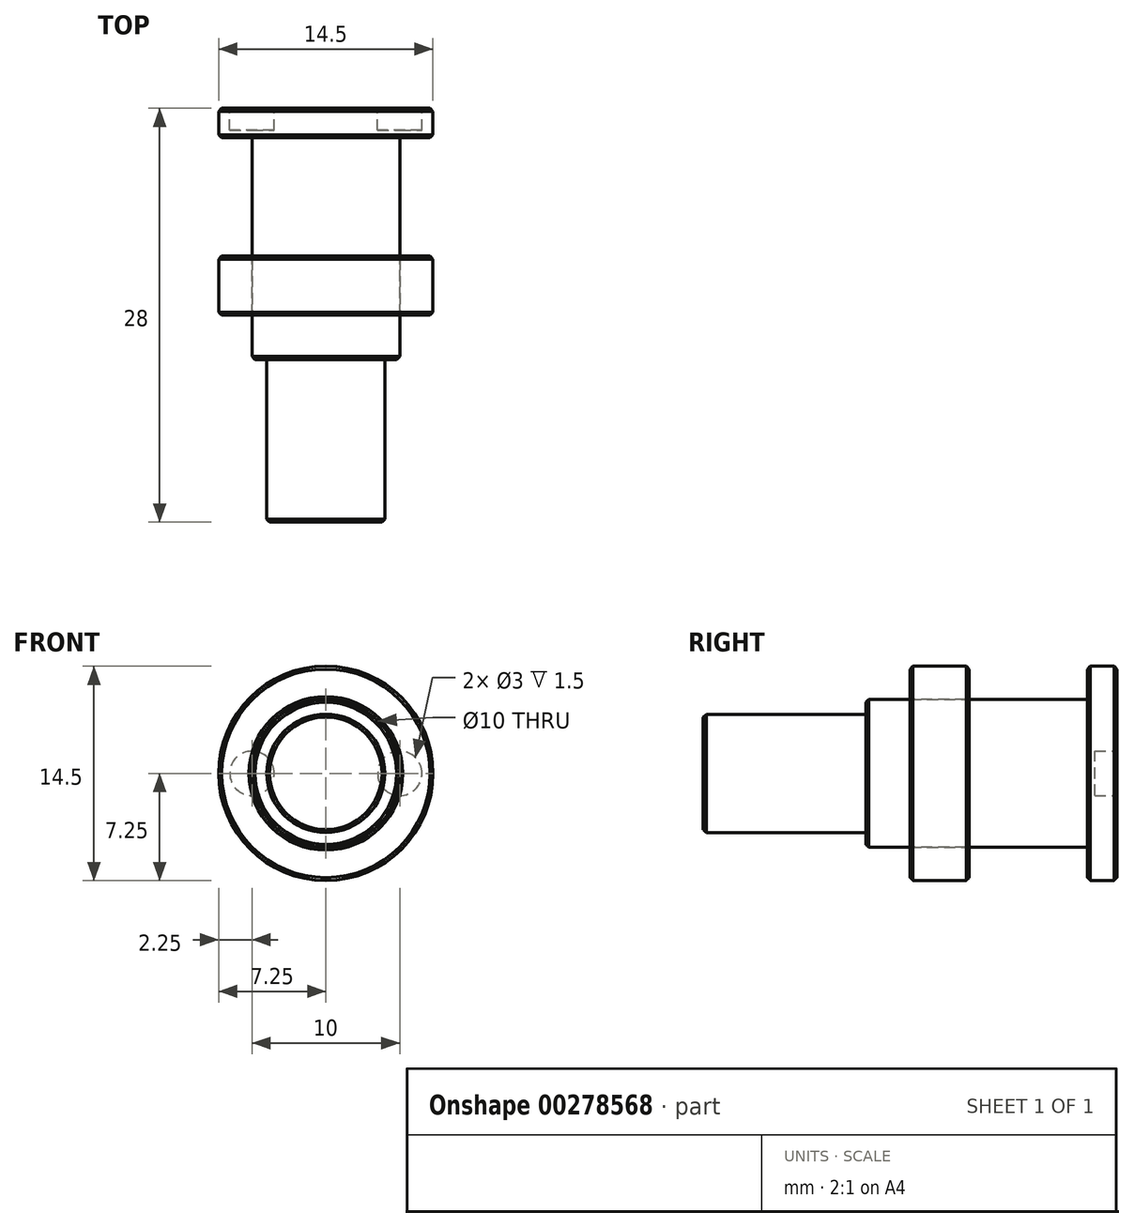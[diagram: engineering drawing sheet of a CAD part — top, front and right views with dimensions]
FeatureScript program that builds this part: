
annotation { "Feature Type Name" : "Feature", "Feature Type Description" : "" }
export const myFeature = defineFeature(function(context is Context, id is Id, definition is map)
    precondition{}
    {
        {
            var Q0;
            Q0=qCreatedBy(makeId("Front.planeOp"),FACE);
            var sketch = newSketch(context, id + "F0", { "sketchPlane" : qUnion([Q0])});
            skCircle(sketch, "E0", {"center": v(0, 0) * mm, "radius": 7.25 * mm});
            skCircle(sketch, "E1", {"center": v(0, 0) * mm, "radius": 5 * mm});
            skCircle(sketch, "E2", {"center": v(0, 0) * mm, "radius": 4 * mm});
            skCircle(sketch, "E3", {"center": v(5, 0) * mm, "radius": 1.5 * mm});
            skCircle(sketch, "E4.1.1", {"center": v(-5, 0) * mm, "radius": 1.5 * mm});
            skSolve(sketch);
        }
        {
            var Q0;
            Q0=makeQuery(id+"F0.imprint","IMPRINT",FACE,{"disambiguationData":[TD([[makeQuery(id+"F0.imprint","IMPRINT",EDGE,{"derivedFrom":sQuery(id+"F0.wireOp",EDGE,"E0")}),1.0]])]});
            var Q1;
            Q1=makeQuery(id+"F0.imprint","IMPRINT",FACE,{"disambiguationData":[TD([[makeQuery(id+"F0.imprint","IMPRINT",EDGE,{"derivedFrom":sQuery(id+"F0.wireOp",EDGE,"E1")}),1.0]])]});
            var Q2;
            Q2=makeQuery(id+"F0.imprint","IMPRINT",FACE,{"disambiguationData":[TD([[makeQuery(id+"F0.imprint","IMPRINT",EDGE,{"derivedFrom":sQuery(id+"F0.wireOp",EDGE,"E0")}),1.0]])]});
            var Q3;
            {var subQ0=sQuery(id+"F0.wireOp",EDGE,"E4.1.1");var subQ1=sQuery(id+"F0.wireOp",EDGE,"E1");var subQ2=makeQuery(id+"F0.imprint","INTERSECT",VERTEX,{"disambiguationData":[OD(0.0)],"derivedFrom":[subQ1,subQ0]});Q3=makeQuery(id+"F0.imprint","IMPRINT",FACE,{"disambiguationData":[TD([[makeQuery(id+"F0.imprint","IMPRINT",EDGE,{"disambiguationData":[TD([[subQ2,-1.0]])],"derivedFrom":subQ1}),-1.0]])]});}
            var Q4;
            {var subQ0=sQuery(id+"F0.wireOp",EDGE,"E3");var subQ1=sQuery(id+"F0.wireOp",EDGE,"E1");var subQ2=makeQuery(id+"F0.imprint","INTERSECT",VERTEX,{"disambiguationData":[OD(0.0)],"derivedFrom":[subQ1,subQ0]});Q4=makeQuery(id+"F0.imprint","IMPRINT",FACE,{"disambiguationData":[TD([[makeQuery(id+"F0.imprint","IMPRINT",EDGE,{"disambiguationData":[TD([[subQ2,1.0]])],"derivedFrom":subQ1}),1.0]])]});}
            var Q5;
            {var subQ0=sQuery(id+"F0.wireOp",EDGE,"E3");var subQ1=sQuery(id+"F0.wireOp",EDGE,"E1");var subQ2=makeQuery(id+"F0.imprint","INTERSECT",VERTEX,{"disambiguationData":[OD(0.0)],"derivedFrom":[subQ1,subQ0]});Q5=makeQuery(id+"F0.imprint","IMPRINT",FACE,{"disambiguationData":[TD([[makeQuery(id+"F0.imprint","IMPRINT",EDGE,{"disambiguationData":[TD([[subQ2,1.0]])],"derivedFrom":subQ1}),-1.0]])]});}
            var Q6;
            {var subQ0=sQuery(id+"F0.wireOp",EDGE,"E4.1.1");var subQ1=sQuery(id+"F0.wireOp",EDGE,"E1");var subQ2=makeQuery(id+"F0.imprint","INTERSECT",VERTEX,{"disambiguationData":[OD(0.0)],"derivedFrom":[subQ1,subQ0]});Q6=makeQuery(id+"F0.imprint","IMPRINT",FACE,{"disambiguationData":[TD([[makeQuery(id+"F0.imprint","IMPRINT",EDGE,{"disambiguationData":[TD([[subQ2,-1.0]])],"derivedFrom":subQ1}),1.0]])]});}
            var Q7;
            {var subQ0=sQuery(id+"F0.wireOp",EDGE,"E3");var subQ1=sQuery(id+"F0.wireOp",EDGE,"E2");var subQ2=makeQuery(id+"F0.imprint","INTERSECT",VERTEX,{"disambiguationData":[OD(0.0)],"derivedFrom":[subQ1,subQ0]});Q7=makeQuery(id+"F0.imprint","IMPRINT",FACE,{"disambiguationData":[TD([[makeQuery(id+"F0.imprint","IMPRINT",EDGE,{"disambiguationData":[TD([[subQ2,1.0]])],"derivedFrom":subQ1}),1.0]])]});}
            var Q8;
            {var subQ0=sQuery(id+"F0.wireOp",EDGE,"E4.1.1");var subQ1=sQuery(id+"F0.wireOp",EDGE,"E2");var subQ2=makeQuery(id+"F0.imprint","INTERSECT",VERTEX,{"disambiguationData":[OD(0.0)],"derivedFrom":[subQ1,subQ0]});Q8=makeQuery(id+"F0.imprint","IMPRINT",FACE,{"disambiguationData":[TD([[makeQuery(id+"F0.imprint","IMPRINT",EDGE,{"disambiguationData":[TD([[subQ2,-1.0]])],"derivedFrom":subQ1}),1.0]])]});}
            var Q9;
            {var subQ0=sQuery(id+"F0.wireOp",EDGE,"E4.1.1");var subQ1=sQuery(id+"F0.wireOp",EDGE,"E2");var subQ2=makeQuery(id+"F0.imprint","INTERSECT",VERTEX,{"disambiguationData":[OD(0.0)],"derivedFrom":[subQ1,subQ0]});Q9=makeQuery(id+"F0.imprint","IMPRINT",FACE,{"disambiguationData":[TD([[makeQuery(id+"F0.imprint","IMPRINT",EDGE,{"disambiguationData":[TD([[subQ2,1.0]])],"derivedFrom":subQ1}),1.0]])]});}
            extrude(context, id + "F1", {"entities" : qUnion([Q0, Q1, Q2, Q3, Q4, Q5, Q6, Q7, Q8, Q9]), "depth" : 2 * mm});
        }
        {
            var Q0;
            {var subQ0=sQuery(id+"F0.wireOp",EDGE,"E4.1.1");var subQ1=sQuery(id+"F0.wireOp",EDGE,"E2");var subQ2=makeQuery(id+"F0.imprint","INTERSECT",VERTEX,{"disambiguationData":[OD(0.0)],"derivedFrom":[subQ1,subQ0]});Q0=makeQuery(id+"F0.imprint","IMPRINT",FACE,{"disambiguationData":[TD([[makeQuery(id+"F0.imprint","IMPRINT",EDGE,{"disambiguationData":[TD([[subQ2,1.0]])],"derivedFrom":subQ1}),1.0]])]});}
            var Q1;
            {var subQ0=sQuery(id+"F0.wireOp",EDGE,"E3");var subQ1=sQuery(id+"F0.wireOp",EDGE,"E2");var subQ2=makeQuery(id+"F0.imprint","INTERSECT",VERTEX,{"disambiguationData":[OD(0.0)],"derivedFrom":[subQ1,subQ0]});Q1=makeQuery(id+"F0.imprint","IMPRINT",FACE,{"disambiguationData":[TD([[makeQuery(id+"F0.imprint","IMPRINT",EDGE,{"disambiguationData":[TD([[subQ2,1.0]])],"derivedFrom":subQ1}),1.0]])]});}
            var Q2;
            {var subQ0=sQuery(id+"F0.wireOp",EDGE,"E4.1.1");var subQ1=sQuery(id+"F0.wireOp",EDGE,"E1");var subQ2=makeQuery(id+"F0.imprint","INTERSECT",VERTEX,{"disambiguationData":[OD(1.0)],"derivedFrom":[subQ1,subQ0]});Q2=makeQuery(id+"F0.imprint","IMPRINT",FACE,{"disambiguationData":[TD([[makeQuery(id+"F0.imprint","IMPRINT",EDGE,{"disambiguationData":[TD([[subQ2,-1.0]])],"derivedFrom":subQ1}),1.0]])]});}
            var Q3;
            {var subQ0=sQuery(id+"F0.wireOp",EDGE,"E4.1.1");var subQ1=sQuery(id+"F0.wireOp",EDGE,"E1");var subQ2=makeQuery(id+"F0.imprint","INTERSECT",VERTEX,{"disambiguationData":[OD(0.0)],"derivedFrom":[subQ1,subQ0]});Q3=makeQuery(id+"F0.imprint","IMPRINT",FACE,{"disambiguationData":[TD([[makeQuery(id+"F0.imprint","IMPRINT",EDGE,{"disambiguationData":[TD([[subQ2,1.0]])],"derivedFrom":subQ1}),1.0]])]});}
            var Q4;
            {var subQ0=sQuery(id+"F0.wireOp",EDGE,"E4.1.1");var subQ1=sQuery(id+"F0.wireOp",EDGE,"E2");var subQ2=makeQuery(id+"F0.imprint","INTERSECT",VERTEX,{"disambiguationData":[OD(0.0)],"derivedFrom":[subQ1,subQ0]});Q4=makeQuery(id+"F0.imprint","IMPRINT",FACE,{"disambiguationData":[TD([[makeQuery(id+"F0.imprint","IMPRINT",EDGE,{"disambiguationData":[TD([[subQ2,-1.0]])],"derivedFrom":subQ1}),1.0]])]});}
            var Q5;
            {var subQ0=sQuery(id+"F0.wireOp",EDGE,"E4.1.1");var subQ1=sQuery(id+"F0.wireOp",EDGE,"E1");var subQ2=makeQuery(id+"F0.imprint","INTERSECT",VERTEX,{"disambiguationData":[OD(0.0)],"derivedFrom":[subQ1,subQ0]});Q5=makeQuery(id+"F0.imprint","IMPRINT",FACE,{"disambiguationData":[TD([[makeQuery(id+"F0.imprint","IMPRINT",EDGE,{"disambiguationData":[TD([[subQ2,-1.0]])],"derivedFrom":subQ1}),1.0]])]});}
            var Q6;
            {var subQ0=sQuery(id+"F0.wireOp",EDGE,"E3");var subQ1=sQuery(id+"F0.wireOp",EDGE,"E1");var subQ2=makeQuery(id+"F0.imprint","INTERSECT",VERTEX,{"disambiguationData":[OD(0.0)],"derivedFrom":[subQ1,subQ0]});Q6=makeQuery(id+"F0.imprint","IMPRINT",FACE,{"disambiguationData":[TD([[makeQuery(id+"F0.imprint","IMPRINT",EDGE,{"disambiguationData":[TD([[subQ2,1.0]])],"derivedFrom":subQ1}),1.0]])]});}
            extrude(context, id + "F2", {"entities" : qUnion([Q0, Q1, Q2, Q3, Q4, Q5, Q6]), "operationType" : NewBodyOperationType.ADD, "depth" : 17 * mm});
        }
        {
            var Q0;
            {var subQ0=sQuery(id+"F0.wireOp",EDGE,"E3");var subQ1=sQuery(id+"F0.wireOp",EDGE,"E2");var subQ2=makeQuery(id+"F0.imprint","INTERSECT",VERTEX,{"disambiguationData":[OD(0.0)],"derivedFrom":[subQ1,subQ0]});Q0=makeQuery(id+"F0.imprint","IMPRINT",FACE,{"disambiguationData":[TD([[makeQuery(id+"F0.imprint","IMPRINT",EDGE,{"disambiguationData":[TD([[subQ2,1.0]])],"derivedFrom":subQ1}),1.0]])]});}
            var Q1;
            {var subQ0=sQuery(id+"F0.wireOp",EDGE,"E4.1.1");var subQ1=sQuery(id+"F0.wireOp",EDGE,"E2");var subQ2=makeQuery(id+"F0.imprint","INTERSECT",VERTEX,{"disambiguationData":[OD(0.0)],"derivedFrom":[subQ1,subQ0]});Q1=makeQuery(id+"F0.imprint","IMPRINT",FACE,{"disambiguationData":[TD([[makeQuery(id+"F0.imprint","IMPRINT",EDGE,{"disambiguationData":[TD([[subQ2,1.0]])],"derivedFrom":subQ1}),1.0]])]});}
            var Q2;
            {var subQ0=sQuery(id+"F0.wireOp",EDGE,"E4.1.1");var subQ1=sQuery(id+"F0.wireOp",EDGE,"E2");var subQ2=makeQuery(id+"F0.imprint","INTERSECT",VERTEX,{"disambiguationData":[OD(0.0)],"derivedFrom":[subQ1,subQ0]});Q2=makeQuery(id+"F0.imprint","IMPRINT",FACE,{"disambiguationData":[TD([[makeQuery(id+"F0.imprint","IMPRINT",EDGE,{"disambiguationData":[TD([[subQ2,-1.0]])],"derivedFrom":subQ1}),1.0]])]});}
            extrude(context, id + "F3", {"entities" : qUnion([Q0, Q1, Q2]), "operationType" : NewBodyOperationType.ADD, "depth" : 28 * mm});
        }
        {
            var Q0;
            {var subQ0=sQuery(id+"F0.wireOp",EDGE,"E4.1.1");var subQ1=sQuery(id+"F0.wireOp",EDGE,"E2");var subQ2=makeQuery(id+"F0.imprint","INTERSECT",VERTEX,{"disambiguationData":[OD(0.0)],"derivedFrom":[subQ1,subQ0]});Q0=makeQuery(id+"F0.imprint","IMPRINT",FACE,{"disambiguationData":[TD([[makeQuery(id+"F0.imprint","IMPRINT",EDGE,{"disambiguationData":[TD([[subQ2,-1.0]])],"derivedFrom":subQ1}),1.0]])]});}
            var Q1;
            {var subQ0=sQuery(id+"F0.wireOp",EDGE,"E4.1.1");var subQ1=sQuery(id+"F0.wireOp",EDGE,"E1");var subQ2=makeQuery(id+"F0.imprint","INTERSECT",VERTEX,{"disambiguationData":[OD(0.0)],"derivedFrom":[subQ1,subQ0]});Q1=makeQuery(id+"F0.imprint","IMPRINT",FACE,{"disambiguationData":[TD([[makeQuery(id+"F0.imprint","IMPRINT",EDGE,{"disambiguationData":[TD([[subQ2,-1.0]])],"derivedFrom":subQ1}),1.0]])]});}
            var Q2;
            {var subQ0=sQuery(id+"F0.wireOp",EDGE,"E3");var subQ1=sQuery(id+"F0.wireOp",EDGE,"E1");var subQ2=makeQuery(id+"F0.imprint","INTERSECT",VERTEX,{"disambiguationData":[OD(0.0)],"derivedFrom":[subQ1,subQ0]});Q2=makeQuery(id+"F0.imprint","IMPRINT",FACE,{"disambiguationData":[TD([[makeQuery(id+"F0.imprint","IMPRINT",EDGE,{"disambiguationData":[TD([[subQ2,1.0]])],"derivedFrom":subQ1}),-1.0]])]});}
            var Q3;
            {var subQ0=sQuery(id+"F0.wireOp",EDGE,"E3");var subQ1=sQuery(id+"F0.wireOp",EDGE,"E1");var subQ2=makeQuery(id+"F0.imprint","INTERSECT",VERTEX,{"disambiguationData":[OD(0.0)],"derivedFrom":[subQ1,subQ0]});Q3=makeQuery(id+"F0.imprint","IMPRINT",FACE,{"disambiguationData":[TD([[makeQuery(id+"F0.imprint","IMPRINT",EDGE,{"disambiguationData":[TD([[subQ2,1.0]])],"derivedFrom":subQ1}),1.0]])]});}
            var Q4;
            {var subQ0=sQuery(id+"F0.wireOp",EDGE,"E3");var subQ1=sQuery(id+"F0.wireOp",EDGE,"E2");var subQ2=makeQuery(id+"F0.imprint","INTERSECT",VERTEX,{"disambiguationData":[OD(0.0)],"derivedFrom":[subQ1,subQ0]});Q4=makeQuery(id+"F0.imprint","IMPRINT",FACE,{"disambiguationData":[TD([[makeQuery(id+"F0.imprint","IMPRINT",EDGE,{"disambiguationData":[TD([[subQ2,1.0]])],"derivedFrom":subQ1}),1.0]])]});}
            var Q5;
            {var subQ0=sQuery(id+"F0.wireOp",EDGE,"E4.1.1");var subQ1=sQuery(id+"F0.wireOp",EDGE,"E1");var subQ2=makeQuery(id+"F0.imprint","INTERSECT",VERTEX,{"disambiguationData":[OD(0.0)],"derivedFrom":[subQ1,subQ0]});Q5=makeQuery(id+"F0.imprint","IMPRINT",FACE,{"disambiguationData":[TD([[makeQuery(id+"F0.imprint","IMPRINT",EDGE,{"disambiguationData":[TD([[subQ2,-1.0]])],"derivedFrom":subQ1}),-1.0]])]});}
            extrude(context, id + "F4", {"entities" : qUnion([Q0, Q1, Q2, Q3, Q4, Q5]), "operationType" : NewBodyOperationType.REMOVE, "depth" : 1.5 * mm});
        }
        {
            var Q0;
            Q0=makeQuery(id+"F1.opExtrude","CAP_EDGE",EDGE,{"disambiguationData":[OSD([sQuery(id+"F0.wireOp",EDGE,"E0")])],"isStart":true});
            var Q1;
            Q1=makeQuery(id+"F1.opExtrude","CAP_EDGE",EDGE,{"disambiguationData":[OSD([sQuery(id+"F0.wireOp",EDGE,"E0")])],"isStart":false});
            var Q2;
            Q2=makeQuery(id+"F4.boolean.opBoolean","COPY",EDGE,{"derivedFrom":makeQuery(id+"F4.opExtrude","CAP_EDGE",EDGE,{"disambiguationData":[OSD([sQuery(id+"F0.wireOp",EDGE,"E3")])],"isStart":true})});
            var Q3;
            Q3=makeQuery(id+"F4.boolean.opBoolean","COPY",EDGE,{"derivedFrom":makeQuery(id+"F4.opExtrude","CAP_EDGE",EDGE,{"disambiguationData":[OSD([sQuery(id+"F0.wireOp",EDGE,"E4.1.1")])],"isStart":true})});
            var Q4;
            Q4=makeQuery(id+"F2.opExtrude","CAP_EDGE",EDGE,{"disambiguationData":[OSD([sQuery(id+"F0.wireOp",EDGE,"E1")])],"isStart":false});
            var Q5;
            Q5=makeQuery(id+"F3.opExtrude","CAP_EDGE",EDGE,{"disambiguationData":[OSD([sQuery(id+"F0.wireOp",EDGE,"E2")])],"isStart":false});
            chamfer(context, id + "F5", {"entities" : qUnion([Q0, Q1, Q2, Q3, Q4, Q5]), "width" : 0.2 * mm, "tangentPropagation" : true});
        }
        {
            var Q0;
            Q0=makeQuery(id+"F2.opExtrude","CAP_FACE",FACE,{"disambiguationData":[OSD([sQuery(id+"F0.wireOp",EDGE,"E1")])],"isStart":false});
            var sketch = newSketch(context, id + "F6", { "sketchPlane" : qUnion([Q0])});
            skCircle(sketch, "E5", {"center": v(0, 0) * mm, "radius": 5 * mm});
            skCircle(sketch, "E6", {"center": v(0, 0) * mm, "radius": 7.25 * mm});
            skSolve(sketch);
        }
        {
            var Q0;
            Q0=makeQuery(id+"F6.imprint","IMPRINT",FACE,{"disambiguationData":[TD([[makeQuery(id+"F6.imprint","IMPRINT",EDGE,{"derivedFrom":sQuery(id+"F6.wireOp",EDGE,"E5")}),-1.0]])]});
            extrude(context, id + "F7", {"entities" : qUnion([Q0]), "oppositeDirection" : true, "depth" : 7 * mm, "hasSecondDirection" : true, "secondDirectionOppositeDirection" : true, "secondDirectionDepth" : 3 * mm});
        }
        {
            var Q0;
            Q0=makeQuery(id+"F7.opExtrude","CAP_EDGE",EDGE,{"disambiguationData":[OSD([sQuery(id+"F6.wireOp",EDGE,"E5")])],"isStart":true});
            var Q1;
            Q1=makeQuery(id+"F7.opExtrude","CAP_EDGE",EDGE,{"disambiguationData":[OSD([sQuery(id+"F6.wireOp",EDGE,"E6")])],"isStart":true});
            var Q2;
            Q2=makeQuery(id+"F7.opExtrude","CAP_EDGE",EDGE,{"disambiguationData":[OSD([sQuery(id+"F6.wireOp",EDGE,"E5")])],"isStart":false});
            var Q3;
            Q3=makeQuery(id+"F7.opExtrude","CAP_EDGE",EDGE,{"disambiguationData":[OSD([sQuery(id+"F6.wireOp",EDGE,"E6")])],"isStart":false});
            chamfer(context, id + "F8", {"entities" : qUnion([Q0, Q1, Q2, Q3]), "width" : 0.2 * mm, "tangentPropagation" : true});
        }
    });
